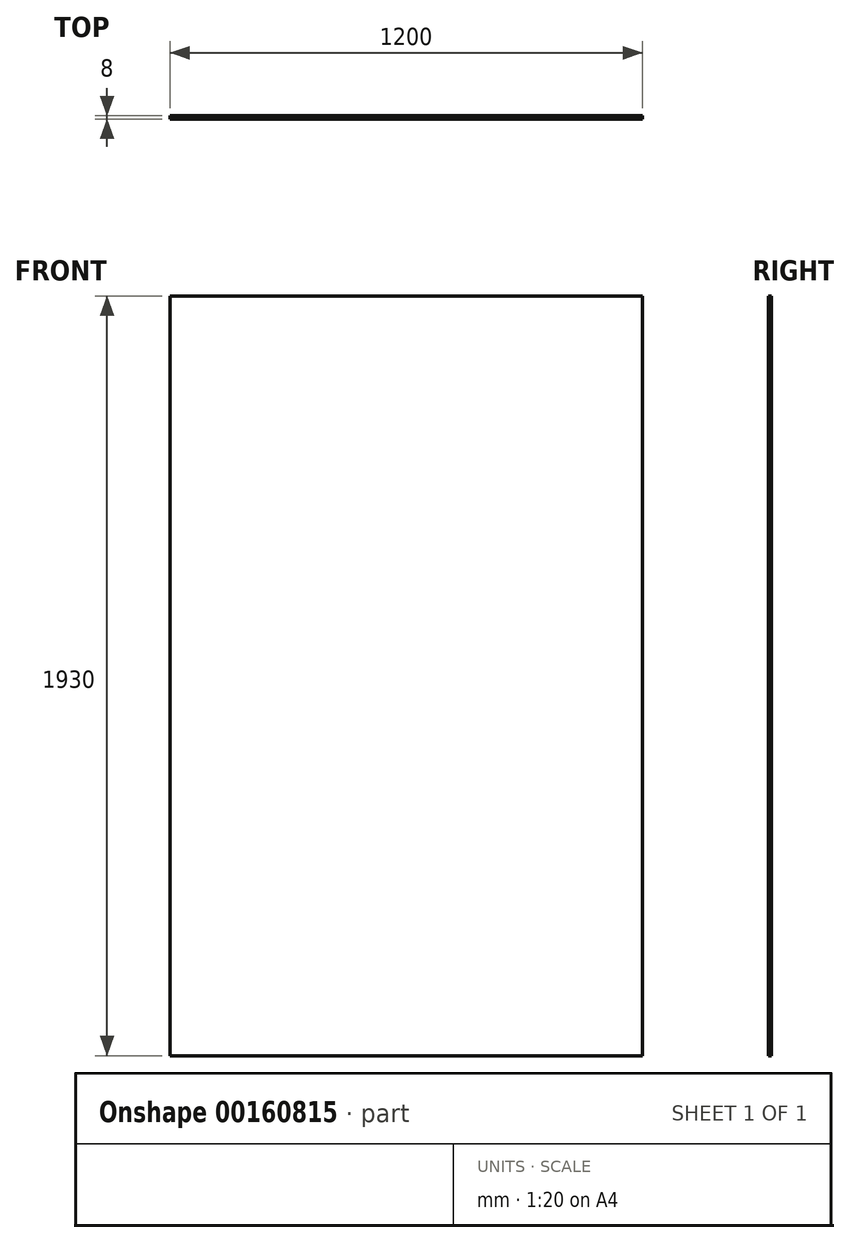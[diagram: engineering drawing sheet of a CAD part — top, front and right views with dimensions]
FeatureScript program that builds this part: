
annotation { "Feature Type Name" : "Feature", "Feature Type Description" : "" }
export const myFeature = defineFeature(function(context is Context, id is Id, definition is map)
    precondition{}
    {
        {
            var Q0;
            Q0=qCreatedBy(makeId("Front.planeOp"),FACE);
            var sketch = newSketch(context, id + "F0", { "sketchPlane" : qUnion([Q0])});
            skLineSegment(sketch, "E0.bottom", {"start": v(0, 0) * mm, "end": v(1200, 0) * mm});
            skLineSegment(sketch, "E0.top", {"start": v(0, 1930) * mm, "end": v(1200, 1930) * mm});
            skLineSegment(sketch, "E0.left", {"start": v(0, 0) * mm, "end": v(0, 1930) * mm});
            skLineSegment(sketch, "E0.right", {"start": v(1200, 0) * mm, "end": v(1200, 1930) * mm});
            skSolve(sketch);
        }
        {
            var Q0;
            Q0=qSketchRegion(id+"F0",true);
            extrude(context, id + "F1", {"entities" : qUnion([Q0]), "depth" : 8 * mm});
        }
    });
